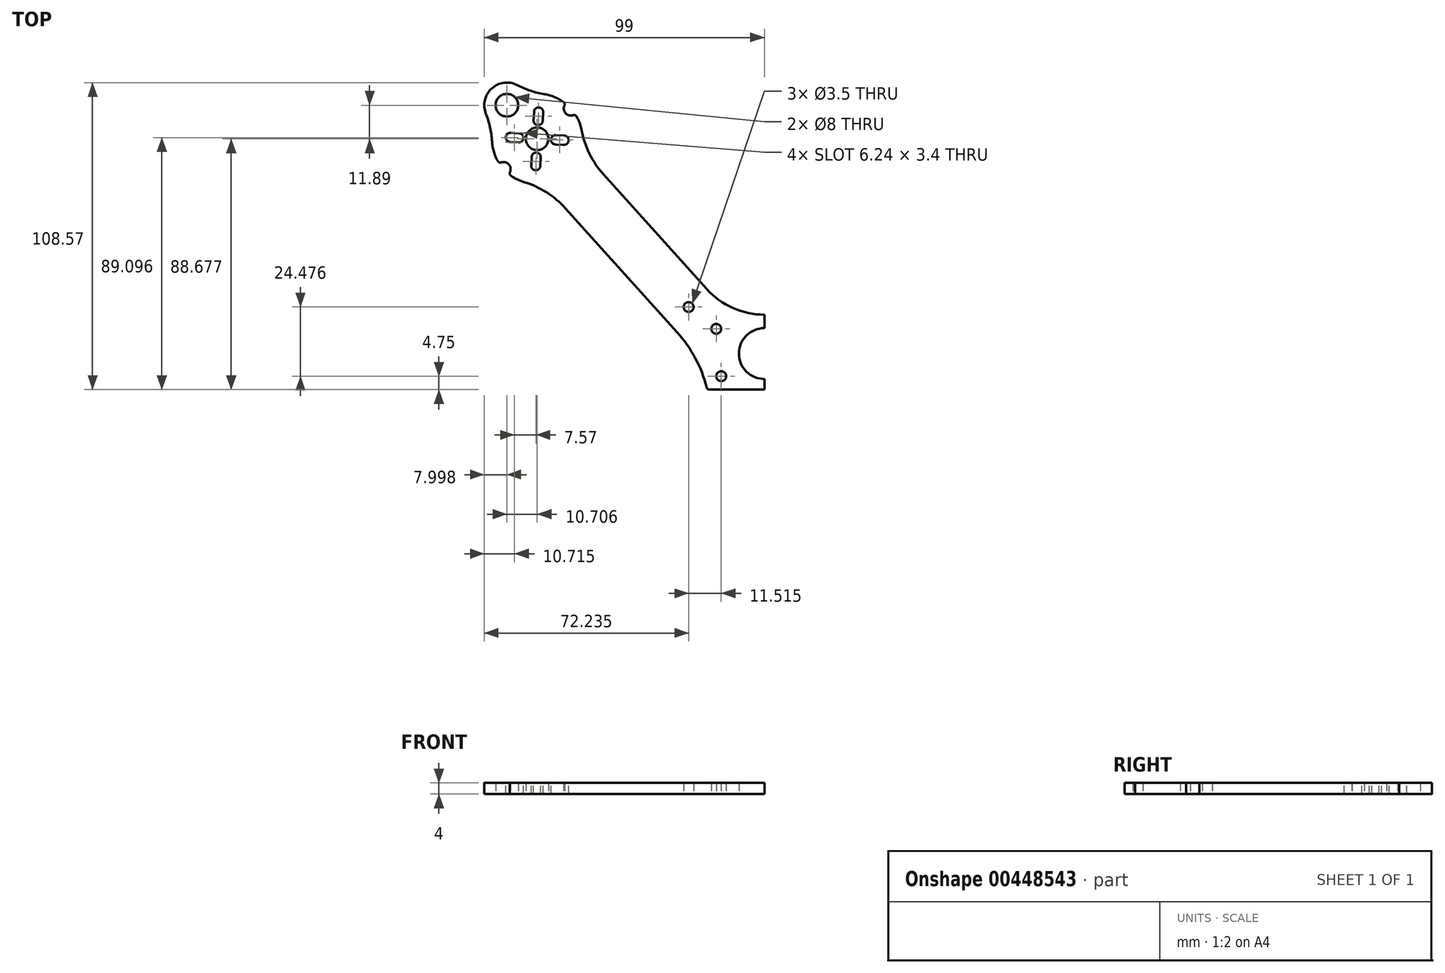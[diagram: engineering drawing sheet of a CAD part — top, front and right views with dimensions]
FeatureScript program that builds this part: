
annotation { "Feature Type Name" : "Feature", "Feature Type Description" : "" }
export const myFeature = defineFeature(function(context is Context, id is Id, definition is map)
    precondition{}
    {
        {
            var Q0;
            Q0=qCreatedBy(makeId("Top.planeOp"),FACE);
            var sketch = newSketch(context, id + "F0", { "sketchPlane" : qUnion([Q0])});
            skLineSegment(sketch, "E0", {"start": v(0, 10) * mm, "end": v(-80.3, 99.18) * mm, "construction": true});
            skCircle(sketch, "E1", {"center": v(-17, 32) * mm, "radius": 1.75 * mm});
            skCircle(sketch, "E2", {"center": v(-15.25, 15.25) * mm, "radius": 1.75 * mm});
            skLineSegment(sketch, "E3", {"start": v(-70.28, 74.6) * mm, "end": v(-30.81, 30.77) * mm});
            skLineSegment(sketch, "E4", {"start": v(-56.9, 86.65) * mm, "end": v(-20.36, 46.07) * mm});
            skLineSegment(sketch, "E5", {"start": v(-19.43, 10.5) * mm, "end": v(0, 10.5) * mm});
            skArc(sketch, "E6", {"start": v(-64.57, 102.14) * mm, "mid": v(-65.27, 104.68) * mm, "end": v(-66.38, 107.07) * mm});
            skLineSegment(sketch, "E7.trimOffspring", {"start": v(-78.13, 83.32) * mm, "end": v(-78.13, 83.32) * mm});
            skCircle(sketch, "E8", {"center": v(-80.3, 99.18) * mm, "radius": 14 * mm, "construction": true});
            skCircle(sketch, "E9", {"center": v(-80.3, 99.18) * mm, "radius": 4 * mm});
            skCircle(sketch, "E10", {"center": v(-26.77, 39.73) * mm, "radius": 1.75 * mm});
            skArc(sketch, "E11", {"start": v(-20.4, 11.26) * mm, "mid": v(-24.41, 21.65) * mm, "end": v(-30.81, 30.77) * mm});
            skPoint(sketch, "E12.orphan", {"position": v(-19, 0) * mm});
            skArc(sketch, "E13", {"start": v(-20.36, 46.07) * mm, "mid": v(-11.15, 39.37) * mm, "end": v(0, 37) * mm});
            skLineSegment(sketch, "E14", {"start": v(0, 37) * mm, "end": v(0, 32.25) * mm});
            skArc(sketch, "E15", {"start": v(0, 32.25) * mm, "mid": v(-9, 23.25) * mm, "end": v(0, 14.25) * mm});
            skLineSegment(sketch, "E16.trimOffspring", {"start": v(0, 14.25) * mm, "end": v(0, 10.5) * mm});
            skPoint(sketch, "E17.visualSharp", {"position": v(-20.21, 10.5) * mm});
            skArc(sketch, "E17.filletArc", {"start": v(-20.4, 11.26) * mm, "mid": v(-20.04, 10.71) * mm, "end": v(-19.43, 10.5) * mm});
            skPoint(sketch, "E18.visualSharp", {"position": v(-64.76, 95.37) * mm});
            skArc(sketch, "E18.filletArc", {"start": v(-64.57, 102.14) * mm, "mid": v(-61.8, 93.87) * mm, "end": v(-56.9, 86.65) * mm});
            skPoint(sketch, "E19.visualSharp", {"position": v(-78.13, 83.32) * mm});
            skArc(sketch, "E19.filletArc", {"start": v(-70.28, 74.6) * mm, "mid": v(-76.95, 80.23) * mm, "end": v(-84.88, 83.85) * mm});
            skArc(sketch, "E20", {"start": v(-70.67, 110.95) * mm, "mid": v(-70.26, 108.21) * mm, "end": v(-67.58, 107.52) * mm});
            skArc(sketch, "E21", {"start": v(-89.93, 87.4) * mm, "mid": v(-90.33, 90.14) * mm, "end": v(-93.01, 90.83) * mm});
            skLineSegment(sketch, "E22", {"start": v(-80.3, 99.18) * mm, "end": v(-91, 111.07) * mm, "construction": true});
            skLineSegment(sketch, "E23", {"start": v(-80.3, 99.18) * mm, "end": v(-68.4, 109.88) * mm, "construction": true});
            skLineSegment(sketch, "E24", {"start": v(-80.3, 99.18) * mm, "end": v(-92.19, 88.47) * mm, "construction": true});
            skArc(sketch, "E25.trimOffspring", {"start": v(-70.99, 112.2) * mm, "mid": v(-74.19, 113.97) * mm, "end": v(-77.7, 114.97) * mm});
            skArc(sketch, "E26.trimOffspring", {"start": v(-96.27, 98.25) * mm, "mid": v(-95.64, 94.65) * mm, "end": v(-94.21, 91.28) * mm});
            skArc(sketch, "E27.trimOffspring", {"start": v(-89.6, 86.16) * mm, "mid": v(-87.34, 84.81) * mm, "end": v(-84.88, 83.85) * mm});
            skPoint(sketch, "E28.visualSharp", {"position": v(-93.7, 90.45) * mm});
            skArc(sketch, "E28.filletArc", {"start": v(-94.21, 91.28) * mm, "mid": v(-93.7, 90.84) * mm, "end": v(-93.01, 90.83) * mm});
            skPoint(sketch, "E29.visualSharp", {"position": v(-90.37, 86.75) * mm});
            skArc(sketch, "E29.filletArc", {"start": v(-89.93, 87.4) * mm, "mid": v(-89.99, 86.72) * mm, "end": v(-89.6, 86.16) * mm});
            skPoint(sketch, "E30.visualSharp", {"position": v(-70.22, 111.6) * mm});
            skArc(sketch, "E30.filletArc", {"start": v(-70.67, 110.95) * mm, "mid": v(-70.6, 111.63) * mm, "end": v(-70.99, 112.2) * mm});
            skPoint(sketch, "E31.visualSharp", {"position": v(-66.88, 107.9) * mm});
            skArc(sketch, "E31.filletArc", {"start": v(-66.38, 107.07) * mm, "mid": v(-66.9, 107.52) * mm, "end": v(-67.58, 107.52) * mm});
            skArc(sketch, "E32", {"start": v(-87.3, 118.16) * mm, "mid": v(-96.35, 117.01) * mm, "end": v(-98.44, 108.13) * mm});
            skPoint(sketch, "E33.visualSharp", {"position": v(-83.9, 114.76) * mm});
            skArc(sketch, "E33.filletArc", {"start": v(-87.3, 118.16) * mm, "mid": v(-82.63, 116.18) * mm, "end": v(-77.7, 114.97) * mm});
            skPoint(sketch, "E34.visualSharp", {"position": v(-95.42, 104.4) * mm});
            skArc(sketch, "E34.filletArc", {"start": v(-96.27, 98.25) * mm, "mid": v(-96.96, 103.28) * mm, "end": v(-98.44, 108.13) * mm});
            skCircle(sketch, "E35", {"center": v(-91, 111.07) * mm, "radius": 4 * mm});
            skCircle(sketch, "E36", {"center": v(0, 0) * mm, "radius": 127.6 * mm, "construction": true});
            skCircle(sketch, "E37", {"center": v(-80.3, 99.18) * mm, "radius": 76.75 * mm, "construction": true});
            skLineSegment(sketch, "E38.MirrorCS", {"start": v(0, 10) * mm, "end": v(80.3, 99.18) * mm, "construction": true});
            skCircle(sketch, "E39.MirrorC", {"center": v(80.3, 99.18) * mm, "radius": 76.75 * mm, "construction": true});
            skSolve(sketch);
        }
        {
            var Q0;
            Q0=makeQuery(id+"F0.imprint","IMPRINT",FACE,{"disambiguationData":[TD([[makeQuery(id+"F0.imprint","IMPRINT",EDGE,{"derivedFrom":sQuery(id+"F0.wireOp",EDGE,"E1")}),-1.0]])]});
            extrude(context, id + "F1", {"entities" : qUnion([Q0]), "depth" : 4 * mm});
        }
        {
            var Q0;
            Q0=makeQuery(id+"F1.opExtrude","CAP_FACE",FACE,{"disambiguationData":[OSD([sQuery(id+"F0.wireOp",EDGE,"E1"),sQuery(id+"F0.wireOp",EDGE,"E2"),sQuery(id+"F0.wireOp",EDGE,"E3"),sQuery(id+"F0.wireOp",EDGE,"E4"),sQuery(id+"F0.wireOp",EDGE,"E5"),sQuery(id+"F0.wireOp",EDGE,"E6"),sQuery(id+"F0.wireOp",EDGE,"E9"),sQuery(id+"F0.wireOp",EDGE,"E10"),sQuery(id+"F0.wireOp",EDGE,"E11"),sQuery(id+"F0.wireOp",EDGE,"E13"),sQuery(id+"F0.wireOp",EDGE,"E14"),sQuery(id+"F0.wireOp",EDGE,"E15"),sQuery(id+"F0.wireOp",EDGE,"E16.trimOffspring"),sQuery(id+"F0.wireOp",EDGE,"E17.filletArc"),sQuery(id+"F0.wireOp",EDGE,"E18.filletArc"),sQuery(id+"F0.wireOp",EDGE,"E19.filletArc"),sQuery(id+"F0.wireOp",EDGE,"XlwXw7Ia-4k9A-3DB6-GY0S-PxJLlph5xH7B"),sQuery(id+"F0.wireOp",EDGE,"E20"),sQuery(id+"F0.wireOp",EDGE,"E21"),sQuery(id+"F0.wireOp",EDGE,"E25.trimOffspring"),sQuery(id+"F0.wireOp",EDGE,"E26.trimOffspring"),sQuery(id+"F0.wireOp",EDGE,"E27.trimOffspring"),sQuery(id+"F0.wireOp",EDGE,"465da84a-1fcb-458c-8af7-43b6bd39abb9.filletArc"),sQuery(id+"F0.wireOp",EDGE,"546c875d-b3e8-496f-961f-fee2dbec4bf7.filletArc"),sQuery(id+"F0.wireOp",EDGE,"E28.filletArc"),sQuery(id+"F0.wireOp",EDGE,"E29.filletArc"),sQuery(id+"F0.wireOp",EDGE,"E30.filletArc"),sQuery(id+"F0.wireOp",EDGE,"E31.filletArc")])],"isStart":false});
            var sketch = newSketch(context, id + "F2", { "sketchPlane" : qUnion([Q0])});
            skLineSegment(sketch, "E40", {"start": v(-80.3, 99.18) * mm, "end": v(0, 10) * mm, "construction": true});
            skLineSegment(sketch, "E41", {"start": v(-80.3, 99.18) * mm, "end": v(-73.8, 98.84) * mm, "construction": true});
            skLineSegment(sketch, "E42", {"start": v(-73.8, 98.84) * mm, "end": v(-70.8, 98.68) * mm, "construction": true});
            skArc(sketch, "E43.0.startCap", {"start": v(-73.89, 97.21) * mm, "mid": v(-75.43, 98.92) * mm, "end": v(-73.72, 100.46) * mm});
            skArc(sketch, "E43.0.endCap", {"start": v(-70.72, 100.3) * mm, "mid": v(-69.19, 98.6) * mm, "end": v(-70.9, 97.06) * mm});
            skLineSegment(sketch, "E43.0.left", {"start": v(-73.72, 100.46) * mm, "end": v(-70.72, 100.3) * mm});
            skLineSegment(sketch, "E43.0.right", {"start": v(-73.89, 97.21) * mm, "end": v(-70.9, 97.06) * mm});
            skLineSegment(sketch, "E44.1.0", {"start": v(-81.58, 105.75) * mm, "end": v(-81.42, 108.75) * mm});
            skArc(sketch, "E44.1.1", {"start": v(-78.33, 105.58) * mm, "mid": v(-80.04, 104.05) * mm, "end": v(-81.58, 105.75) * mm});
            skLineSegment(sketch, "E44.1.2", {"start": v(-78.33, 105.58) * mm, "end": v(-78.18, 108.58) * mm});
            skArc(sketch, "E44.1.3", {"start": v(-81.42, 108.75) * mm, "mid": v(-79.71, 110.29) * mm, "end": v(-78.18, 108.58) * mm});
            skLineSegment(sketch, "E44.2.0", {"start": v(-86.87, 97.9) * mm, "end": v(-89.87, 98.05) * mm});
            skArc(sketch, "E44.2.1", {"start": v(-86.7, 101.14) * mm, "mid": v(-85.16, 99.43) * mm, "end": v(-86.87, 97.9) * mm});
            skLineSegment(sketch, "E44.2.2", {"start": v(-86.7, 101.14) * mm, "end": v(-89.7, 101.3) * mm});
            skArc(sketch, "E44.2.3", {"start": v(-89.87, 98.05) * mm, "mid": v(-91.4, 99.76) * mm, "end": v(-89.7, 101.3) * mm});
            skLineSegment(sketch, "E44.3.0", {"start": v(-79.01, 92.6) * mm, "end": v(-79.17, 89.6) * mm});
            skArc(sketch, "E44.3.1", {"start": v(-82.26, 92.77) * mm, "mid": v(-80.55, 94.3) * mm, "end": v(-79.01, 92.6) * mm});
            skLineSegment(sketch, "E44.3.2", {"start": v(-82.26, 92.77) * mm, "end": v(-82.42, 89.78) * mm});
            skArc(sketch, "E44.3.3", {"start": v(-79.17, 89.6) * mm, "mid": v(-80.88, 88.07) * mm, "end": v(-82.42, 89.78) * mm});
            skPoint(sketch, "E44.center", {"position": v(-80.3, 99.18) * mm});
            skSolve(sketch);
        }
        {
            var Q0;
            Q0=qSketchRegion(id+"F2",true);
            extrude(context, id + "F3", {"entities" : qUnion([Q0]), "operationType" : NewBodyOperationType.REMOVE, "oppositeDirection" : true, "depth" : 25 * mm});
        }
    });
